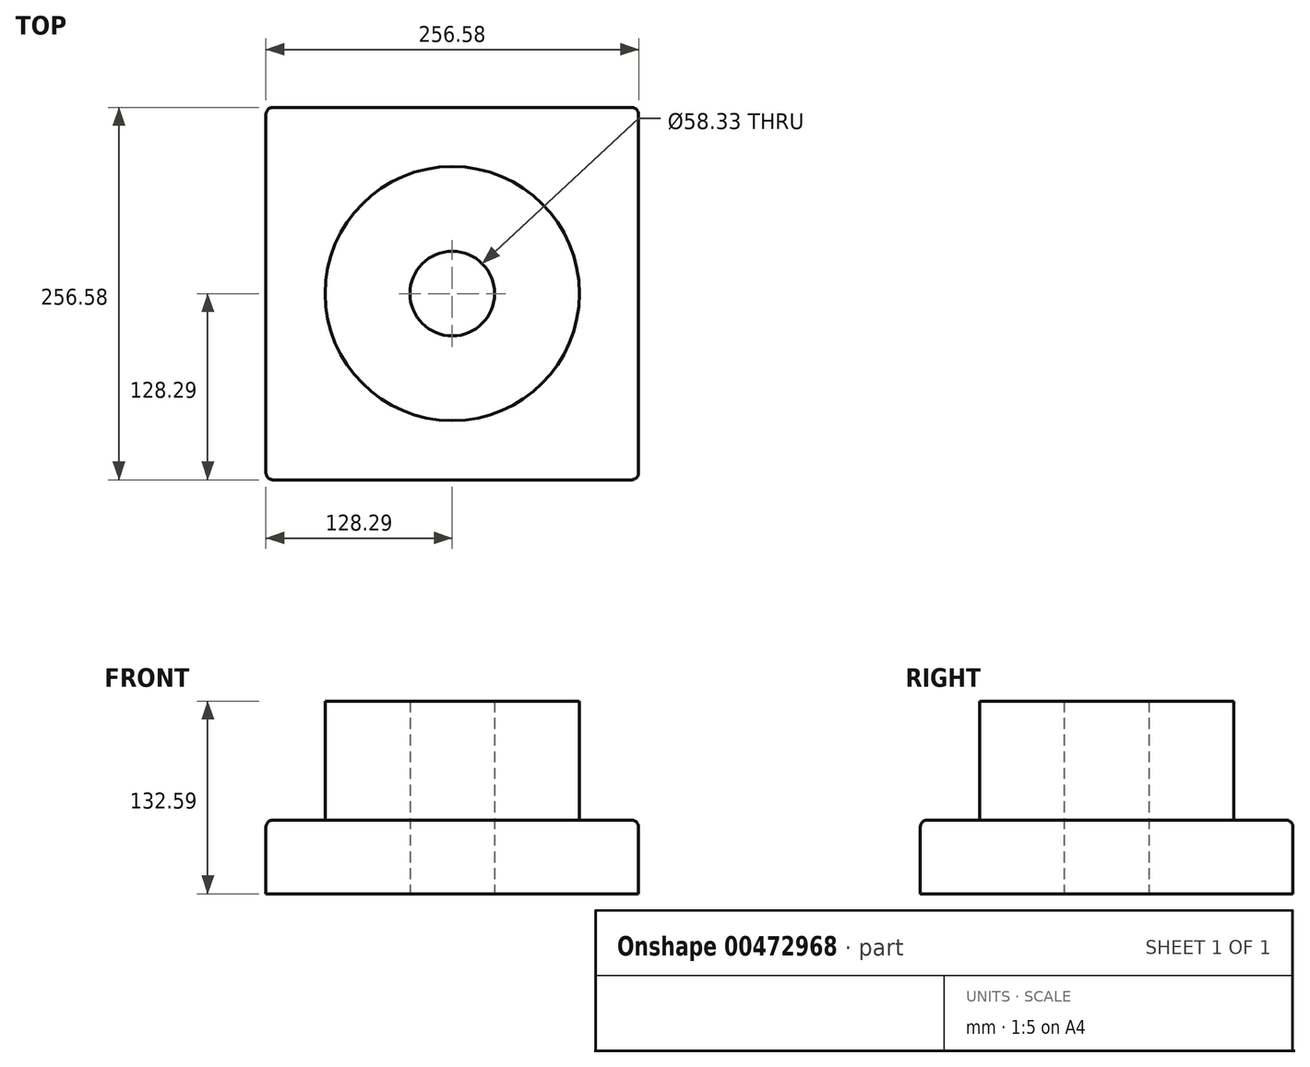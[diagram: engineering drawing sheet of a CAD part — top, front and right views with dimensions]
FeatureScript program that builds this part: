
annotation { "Feature Type Name" : "Feature", "Feature Type Description" : "" }
export const myFeature = defineFeature(function(context is Context, id is Id, definition is map)
    precondition{}
    {
        {
            var Q0;
            Q0=qCreatedBy(makeId("Top.planeOp"),FACE);
            var sketch = newSketch(context, id + "F0", { "sketchPlane" : qUnion([Q0])});
            skLineSegment(sketch, "E0", {"start": v(128.29, -128.29) * mm, "end": v(-128.29, -128.29) * mm});
            skLineSegment(sketch, "E1", {"start": v(-128.29, -128.29) * mm, "end": v(-128.29, 128.29) * mm});
            skLineSegment(sketch, "E2", {"start": v(-128.29, 128.29) * mm, "end": v(128.29, 128.29) * mm});
            skLineSegment(sketch, "E3", {"start": v(128.29, 128.29) * mm, "end": v(128.29, -128.29) * mm});
            skCircle(sketch, "E4", {"center": v(0, 0) * mm, "radius": 128.29 * mm, "construction": true});
            skCircle(sketch, "E5", {"center": v(0, 0) * mm, "radius": 29.16 * mm});
            skSolve(sketch);
        }
        {
            var Q0;
            Q0 = qSketchRegion(id + "F0", true);
            extrude(context, id + "F1", {"entities" : qUnion([Q0]), "depth" : 50.8 * mm});
        }
        {
            var Q0;
            Q0=makeQuery(id+"F1.opExtrude","CAP_EDGE",EDGE,{"disambiguationData":[OSD([sQuery(id+"F0.wireOp",EDGE,"E2")])],"isStart":false});
            fillet(context, id + "F2", {"entities" : qUnion([Q0]), "radius" : 5.08 * mm, "tangentPropagation" : true, "allowEdgeOverflow" : false});
        }
        {
            var Q0;
            Q0=makeQuery(id+"F1.opExtrude","CAP_EDGE",EDGE,{"disambiguationData":[OSD([sQuery(id+"F0.wireOp",EDGE,"E3")])],"isStart":false});
            fillet(context, id + "F3", {"entities" : qUnion([Q0]), "radius" : 5.08 * mm, "tangentPropagation" : true, "allowEdgeOverflow" : false});
        }
        {
            var Q0;
            Q0=makeQuery(id+"F1.opExtrude","CAP_EDGE",EDGE,{"disambiguationData":[OSD([sQuery(id+"F0.wireOp",EDGE,"E0")])],"isStart":false});
            fillet(context, id + "F4", {"entities" : qUnion([Q0]), "radius" : 5.08 * mm, "tangentPropagation" : true, "allowEdgeOverflow" : false});
        }
        {
            var Q0;
            Q0=makeQuery(id+"F1.opExtrude","CAP_EDGE",EDGE,{"disambiguationData":[OSD([sQuery(id+"F0.wireOp",EDGE,"E1")])],"isStart":false});
            fillet(context, id + "F5", {"entities" : qUnion([Q0]), "radius" : 5.08 * mm, "tangentPropagation" : true, "allowEdgeOverflow" : false});
        }
        {
            var Q0;
            Q0=qCreatedBy(makeId("Top.planeOp"),FACE);
            var sketch = newSketch(context, id + "F6", { "sketchPlane" : qUnion([Q0])});
            skCircle(sketch, "E6.0", {"center": v(0, 0) * mm, "radius": 29.16 * mm});
            skCircle(sketch, "E7", {"center": v(0, 0) * mm, "radius": 87.49 * mm});
            skCircle(sketch, "E8", {"center": v(58.33, 0) * mm, "radius": 29.16 * mm, "construction": true});
            skSolve(sketch);
        }
        {
            var Q0;
            Q0 = qSketchRegion(id + "F6", true);
            extrude(context, id + "F7", {"entities" : qUnion([Q0]), "operationType" : NewBodyOperationType.ADD, "depth" : 132.6 * mm});
        }
    });
